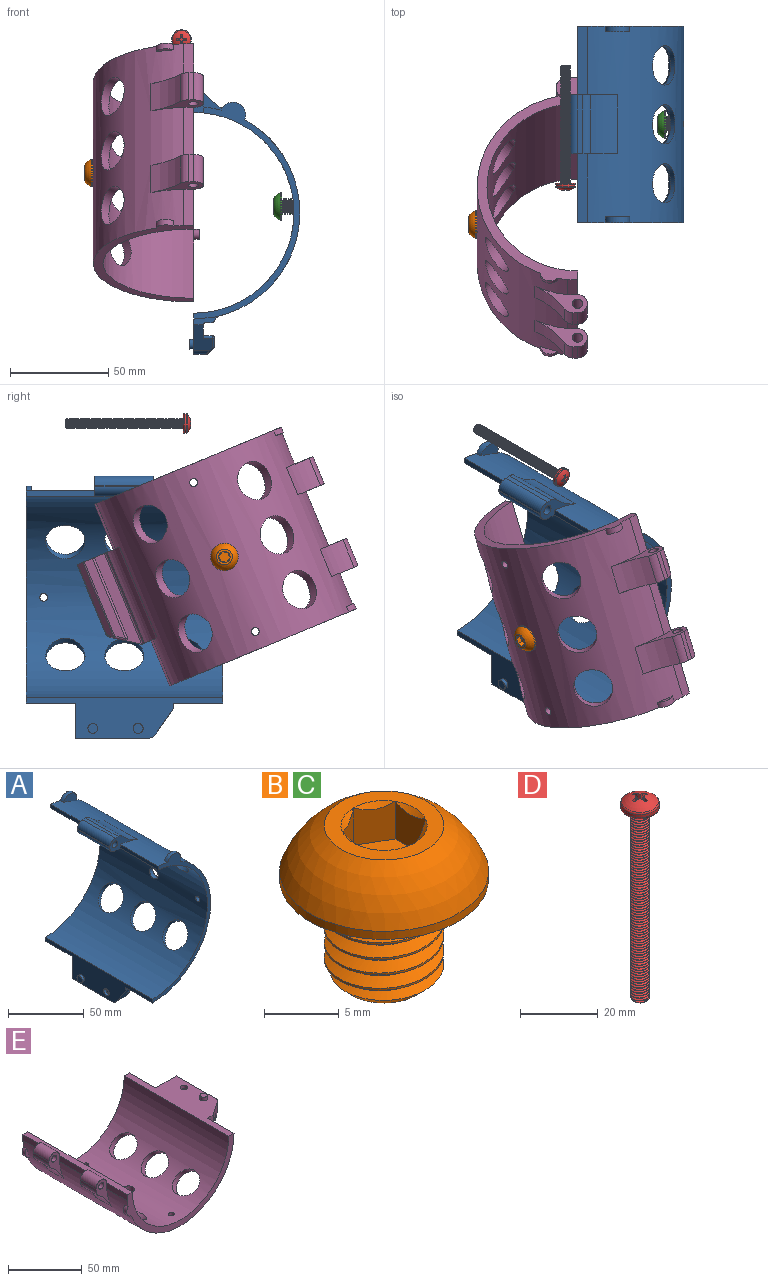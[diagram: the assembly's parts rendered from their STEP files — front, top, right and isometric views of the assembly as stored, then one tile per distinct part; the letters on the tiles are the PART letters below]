
ASSEMBLY  parts=5 mates=2
PART A: 58 faces, bbox 59.1x100x133.4 mm
  f0: cylinder r=54.1mm len=106.94mm, axis (0,1,0), area 12715.4mm2, adj f13,f14,f15,f16,f17,f18,f19,f23
  f1: cylinder r=51.1mm len=102.2mm, axis (0,1,0), area 13703.6mm2, adj f8,f10,f13,f14,f15,f16,f17,f18
  f2: plane 44.23x4.5mm, normal (0,0,1), area 199mm2, adj f3,f26,f28,f40
  f3: plane 50x7.07mm, normal (1,0,0), area 265.2mm2, adj f2,f26,f30,f32,f40
  f4: plane 50x3.5mm, normal (0,0,-1), area 175mm2, adj f24,f26,f29,f30
  f5: plane 36.89x6.59mm, normal (0,0,-1), area 243mm2, adj f8,f26,f33,f34
  f6: plane 41.02x2.91mm, normal (0.71,0,-0.71), area 163.9mm2, adj f26,f27,f34,f35,f36
  f7: plane 44.23x4.59mm, normal (1,0,0), area 195.4mm2, adj f26,f27,f28,f38
  f8: plane 100x20.84mm, normal (-1,0,0), area 1072.3mm2, adj f1,f5,f13,f14,f23,f24,f25,f26
  f9: cylinder r=2.55mm len=30mm, axis (0,1,0), area 480.7mm2, adj f16,f18
  f10: plane 30x0.02mm, normal (0,0,-1), area 0.6mm2, adj f1,f16,f18,f22
  f11: plane 30x2.74mm, normal (0,0,1), area 82.3mm2, adj f16,f18,f20,f21
  f12: plane 30x0.32mm, normal (-1,0,0), area 9.6mm2, adj f16,f18,f21,f22
  f13: plane 110.42x54.1mm, normal (0,-1,0), area 541.2mm2, adj f0,f1,f8,f15,f23,f46
  f14: plane 110.37x54.1mm, normal (0,1,0), area 540.6mm2, adj f0,f1,f8,f17,f25,f48
  f15: plane 35x3.01mm, normal (-1,0,0), area 105.5mm2, adj f0,f1,f13,f16
  f16: plane 25.52x11.37mm, normal (0,-1,0), area 109mm2, adj f0,f1,f9,f10,f11,f12,f15,f19
  f17: plane 35x3.01mm, normal (-1,0,0), area 105.5mm2, adj f0,f1,f14,f18
  f18: plane 25.52x11.37mm, normal (0,1,0), area 109mm2, adj f0,f1,f9,f10,f11,f12,f17,f19
  f19: cylinder r=40mm len=30mm, axis (0,-1,0), area 519.1mm2, adj f0,f16,f18,f20
  f20: cylinder r=5mm len=30mm, axis (0,-1,0), area 123.3mm2, adj f11,f16,f18,f19
  f21: cylinder r=5mm len=30mm, axis (0,1,0), area 235.6mm2, adj f11,f12,f16,f18
  f22: cylinder r=5mm len=30mm, axis (0,-1,0), area 235mm2, adj f10,f12,f16,f18
  f23: plane 25x10.5mm, normal (0.1,0,-1), area 263.8mm2, adj f0,f8,f13,f24
  f24: plane 13.81x4.63mm, normal (0,-1,0), area 31.6mm2, adj f0,f4,f8,f23,f29,f30,f31,f32
  f25: plane 25x10.5mm, normal (0.1,0,-1), area 263.8mm2, adj f0,f8,f14,f26
  f26: plane 19.63x13.81mm, normal (0,1,0), area 152.5mm2, adj f0,f2,f3,f4,f5,f6,f7,f8
  f27: cylinder r=1mm len=41.02mm, axis (0,1,0), area 32.2mm2, adj f6,f7,f26,f37
  f28: cylinder r=1mm len=44.23mm, axis (0,1,0), area 69.5mm2, adj f2,f7,f26,f39
  f29: cylinder r=1mm len=50mm, axis (0,-1,0), area 59.8mm2, adj f4,f24,f26,f31
  f30: cylinder r=1mm len=50mm, axis (0,-1,0), area 78.5mm2, adj f3,f4,f24,f26,f32
  f31: cylinder r=5mm len=50mm, axis (0,-1,0), area 234.3mm2, adj f0,f24,f26,f29
  f32: plane 12.87x9.5mm, normal (0,-0.82,-0.57), area 109.5mm2, adj f3,f8,f24,f30,f33,f36,f38,f40
  f33: cylinder r=5mm len=8.29mm, axis (-1,0,0), area 34.4mm2, adj f5,f8,f32,f35
  f34: cylinder r=1mm len=36.89mm, axis (0,1,0), area 29mm2, adj f5,f6,f26,f35
  f35: bspline ~4.44x2.86mm, area 4.4mm2, adj f6,f33,f34,f36
  f36: cylinder r=1mm len=1.92mm, axis (-0.63,0.44,-0.63), area 2.2mm2, adj f6,f32,f35,f37
  f37: sphere r=1mm, area 0.5mm2, adj f27,f36,f38
  f38: cylinder r=1mm len=5.16mm, axis (0,0.57,-0.82), area 8.8mm2, adj f7,f32,f37,f39
  f39: sphere r=1mm, area 2.2mm2, adj f28,f38,f40
  f40: cylinder r=1mm len=4.5mm, axis (1,0,0), area 9.8mm2, adj f2,f3,f32,f39
  f41: cylinder r=2.55mm len=5.1mm, axis (-1,0,0), area 32mm2, adj f8,f42
  f42: plane 5.1x5.1mm, normal (-1,0,0), area 20.4mm2, adj f41
  f43: cylinder r=2.5mm len=5mm, axis (1,0,0), area 31.4mm2, adj f8,f44
  f44: plane 5x5mm, normal (-1,0,0), area 19.6mm2, adj f43
  f45: cylinder r=4mm len=8mm, axis (-1,0,0), area 75.5mm2, adj f0,f1
  f46: cylinder r=6.46mm len=12.47mm, axis (0,-1,0), area 60.9mm2, adj f0,f13,f47
  f47: plane 12.47x8.87mm, normal (0,1,0), area 62.3mm2, adj f0,f46
  f48: cylinder r=6.47mm len=12.45mm, axis (0,1,0), area 60.6mm2, adj f0,f14,f49
  f49: plane 12.45x8.83mm, normal (0,-1,0), area 61.7mm2, adj f0,f48
  f50: cylinder r=2mm len=4mm, axis (-1,0,0), area 37.7mm2, adj f0,f1
  f51: cylinder r=2mm len=4mm, axis (-1,0,0), area 37.7mm2, adj f0,f1
  f52: cylinder r=10mm len=20mm, axis (-0.71,0,-0.71), area 193.9mm2, adj f0,f1
  f53: cylinder r=10mm len=20mm, axis (-0.71,0,-0.71), area 193.9mm2, adj f0,f1
  f54: cylinder r=10mm len=20mm, axis (-0.71,0,-0.71), area 193.9mm2, adj f0,f1
  f55: cylinder r=10mm len=20mm, axis (-0.71,0,0.71), area 192.6mm2, adj f0,f1
  f56: cylinder r=10mm len=20mm, axis (-0.71,0,0.71), area 192.6mm2, adj f0,f1
  f57: cylinder r=10mm len=20mm, axis (-0.71,0,0.71), area 192.6mm2, adj f0,f1
PART B: 24 faces, bbox 15.1x15.1x13.8 mm
  f0: cylinder r=4mm len=8mm, axis (0,0,-1), area 22.4mm2, adj f1,f5,f22,f23
  f1: bspline ~8.81x8mm, area 126.7mm2, adj f0,f2,f4,f5,f23
  f2: cone r=3.06mm half-angle=45deg, axis (0,0,1), area 12.7mm2, adj f1,f3,f4,f23
  f3: plane 6.13x6.13mm, normal (0,0,-1), area 29.5mm2, adj f2
  f4: cylinder r=3.19mm len=7.87mm, axis (0,0,-1), area 19.9mm2, adj f1,f2,f5,f22
  f5: plane 14.51x14.51mm, normal (0,0,-1), area 113.1mm2, adj f0,f1,f4,f6,f22
  f6: cylinder r=7mm len=14mm, axis (0,0,1), area 29mm2, adj f5,f7
  f7: sphere r=7.45mm, area 175mm2, adj f6,f8
  f8: plane 8.94x8.94mm, normal (0,0,1), area 24.1mm2, adj f7,f9,f17,f18,f19,f20,f21
  f9: cone r=2.89mm half-angle=45deg, axis (0,0,1), area 0mm2, adj f8,f10
  f10: plane 4.17x3.59mm, normal (0.5,0.87,0), area 8.2mm2, adj f9,f11,f15,f16
  f11: plane 5.77x5mm, normal (0,0,1), area 21.7mm2, adj f10,f12,f13,f14,f15,f16
  f12: plane 4.17x3.59mm, normal (0.5,-0.87,0), area 8.2mm2, adj f11,f13,f16,f20
  f13: plane 4.17x3.59mm, normal (-0.5,-0.87,0), area 8.2mm2, adj f11,f12,f14,f19
  f14: plane 4.18x3.99mm, normal (-1,0,0), area 8.2mm2, adj f11,f13,f15,f18
  f15: plane 4.17x3.59mm, normal (-0.5,0.87,0), area 8.2mm2, adj f10,f11,f14,f17
  f16: plane 4.18x3.99mm, normal (1,0,0), area 8.2mm2, adj f10,f11,f12,f21
  f17: cone r=2.89mm half-angle=45deg, axis (0,0,1), area 0mm2, adj f8,f15
  f18: cone r=2.89mm half-angle=45deg, axis (0,0,1), area 0mm2, adj f8,f14
  f19: cone r=2.89mm half-angle=45deg, axis (0,0,1), area 0mm2, adj f8,f13
  f20: cone r=2.89mm half-angle=45deg, axis (0,0,1), area 0mm2, adj f8,f12
  f21: cone r=2.89mm half-angle=45deg, axis (0,0,1), area 0mm2, adj f8,f16
  f22: bspline ~8.59x8mm, area 126.7mm2, adj f0,f4,f5,f23
  f23: cone r=3.06mm half-angle=45deg, axis (0,0,1), area 3.4mm2, adj f0,f1,f2,f22
PART C: same geometry as B
PART D: 182 faces, bbox 11.1x11.1x64.3 mm
  f0: cylinder r=2.5mm len=5mm, axis (0,0,1), area 0.8mm2, adj f75,f76,f150,f151
  f1: cylinder r=2.5mm len=5mm, axis (0,0,1), area 0.8mm2, adj f76,f77,f150,f151
  f2: cylinder r=2.5mm len=5mm, axis (0,0,1), area 0.8mm2, adj f77,f78,f150,f151
  f3: cylinder r=2.5mm len=5mm, axis (0,0,1), area 0.8mm2, adj f78,f79,f150,f151
  f4: cylinder r=2.5mm len=5mm, axis (0,0,1), area 0.8mm2, adj f79,f80,f150,f151
  f5: cylinder r=2.5mm len=5mm, axis (0,0,1), area 0.8mm2, adj f80,f81,f150,f151
  f6: cylinder r=2.5mm len=5mm, axis (0,0,1), area 0.8mm2, adj f81,f82,f150,f151
  f7: cylinder r=2.5mm len=5mm, axis (0,0,1), area 0.8mm2, adj f82,f83,f150,f151
  f8: cylinder r=2.5mm len=5mm, axis (0,0,1), area 0.8mm2, adj f83,f84,f150,f151
  f9: cylinder r=2.5mm len=5mm, axis (0,0,1), area 0.8mm2, adj f84,f85,f150,f151
  f10: cylinder r=2.5mm len=5mm, axis (0,0,1), area 0.8mm2, adj f85,f86,f150,f151
  f11: cylinder r=2.5mm len=5mm, axis (0,0,1), area 0.8mm2, adj f86,f87,f150,f151
  f12: cylinder r=2.5mm len=5mm, axis (0,0,1), area 0.8mm2, adj f87,f88,f150,f151
  f13: cylinder r=2.5mm len=5mm, axis (0,0,1), area 0.8mm2, adj f88,f89,f150,f151
  f14: cylinder r=2.5mm len=5mm, axis (0,0,1), area 0.8mm2, adj f89,f90,f150,f151
  f15: cylinder r=2.5mm len=5mm, axis (0,0,1), area 0.8mm2, adj f90,f91,f150,f151
  f16: cylinder r=2.5mm len=5mm, axis (0,0,1), area 0.8mm2, adj f91,f92,f150,f151
  f17: cylinder r=2.5mm len=5mm, axis (0,0,1), area 0.8mm2, adj f92,f93,f150,f151
  f18: cylinder r=2.5mm len=5mm, axis (0,0,1), area 0.8mm2, adj f93,f94,f150,f151
  f19: cylinder r=2.5mm len=5mm, axis (0,0,1), area 0.8mm2, adj f94,f95,f150,f151
  f20: cylinder r=2.5mm len=5mm, axis (0,0,1), area 0.8mm2, adj f95,f96,f150,f151
  f21: cylinder r=2.5mm len=5mm, axis (0,0,1), area 0.8mm2, adj f96,f97,f150,f151
  f22: cylinder r=2.5mm len=5mm, axis (0,0,1), area 0.8mm2, adj f97,f98,f150,f151
  f23: cylinder r=2.5mm len=5mm, axis (0,0,1), area 0.8mm2, adj f98,f99,f150,f151
  f24: cylinder r=2.5mm len=5mm, axis (0,0,1), area 0.8mm2, adj f99,f100,f150,f151
  f25: cylinder r=2.5mm len=5mm, axis (0,0,1), area 0.8mm2, adj f100,f101,f150,f151
  f26: cylinder r=2.5mm len=5mm, axis (0,0,1), area 0.8mm2, adj f101,f102,f150,f151
  f27: cylinder r=2.5mm len=5mm, axis (0,0,1), area 0.8mm2, adj f102,f103,f150,f151
  f28: cylinder r=2.5mm len=5mm, axis (0,0,1), area 0.8mm2, adj f103,f104,f150,f151
  f29: cylinder r=2.5mm len=5mm, axis (0,0,1), area 0.8mm2, adj f104,f105,f150,f151
  f30: cylinder r=2.5mm len=5mm, axis (0,0,1), area 0.8mm2, adj f105,f106,f150,f151
  f31: cylinder r=2.5mm len=5mm, axis (0,0,1), area 0.8mm2, adj f106,f107,f150,f151
  f32: cylinder r=2.5mm len=5mm, axis (0,0,1), area 0.8mm2, adj f107,f108,f150,f151
  f33: cylinder r=2.5mm len=5mm, axis (0,0,1), area 0.8mm2, adj f108,f109,f150,f151
  f34: cylinder r=2.5mm len=5mm, axis (0,0,1), area 0.8mm2, adj f109,f110,f150,f151
  f35: cylinder r=2.5mm len=5mm, axis (0,0,1), area 0.8mm2, adj f110,f111,f150,f151
  f36: cylinder r=2.5mm len=5mm, axis (0,0,1), area 0.8mm2, adj f111,f112,f150,f151
  f37: cylinder r=2.5mm len=5mm, axis (0,0,1), area 0.8mm2, adj f112,f113,f150,f151
  f38: cylinder r=2.5mm len=5mm, axis (0,0,1), area 0.8mm2, adj f113,f114,f150,f151
  f39: cylinder r=2.5mm len=5mm, axis (0,0,1), area 0.8mm2, adj f114,f115,f150,f151
  f40: cylinder r=2.5mm len=5mm, axis (0,0,1), area 0.8mm2, adj f115,f116,f150,f151
  f41: cylinder r=2.5mm len=5mm, axis (0,0,1), area 0.8mm2, adj f116,f117,f150,f151
  f42: cylinder r=2.5mm len=5mm, axis (0,0,1), area 0.8mm2, adj f117,f118,f150,f151
  f43: cylinder r=2.5mm len=5mm, axis (0,0,1), area 0.8mm2, adj f118,f119,f150,f151
  f44: cylinder r=2.5mm len=5mm, axis (0,0,1), area 0.8mm2, adj f119,f120,f150,f151
  f45: cylinder r=2.5mm len=5mm, axis (0,0,1), area 0.8mm2, adj f120,f121,f150,f151
  f46: cylinder r=2.5mm len=5mm, axis (0,0,1), area 0.8mm2, adj f121,f122,f150,f151
  f47: cylinder r=2.5mm len=5mm, axis (0,0,1), area 0.8mm2, adj f122,f123,f150,f151
  f48: cylinder r=2.5mm len=5mm, axis (0,0,1), area 0.8mm2, adj f123,f124,f150,f151
  f49: cylinder r=2.5mm len=5mm, axis (0,0,1), area 0.8mm2, adj f124,f125,f150,f151
  f50: cylinder r=2.5mm len=5mm, axis (0,0,1), area 0.8mm2, adj f125,f126,f150,f151
  f51: cylinder r=2.5mm len=5mm, axis (0,0,1), area 0.8mm2, adj f126,f127,f150,f151
  f52: cylinder r=2.5mm len=5mm, axis (0,0,1), area 0.8mm2, adj f127,f128,f150,f151
  f53: cylinder r=2.5mm len=5mm, axis (0,0,1), area 0.8mm2, adj f128,f129,f150,f151
  f54: cylinder r=2.5mm len=5mm, axis (0,0,1), area 0.8mm2, adj f129,f130,f150,f151
  f55: cylinder r=2.5mm len=5mm, axis (0,0,1), area 0.8mm2, adj f130,f131,f150,f151
  f56: cylinder r=2.5mm len=5mm, axis (0,0,1), area 0.8mm2, adj f131,f132,f150,f151
  f57: cylinder r=2.5mm len=5mm, axis (0,0,1), area 0.8mm2, adj f132,f133,f150,f151
  f58: cylinder r=2.5mm len=5mm, axis (0,0,1), area 0.8mm2, adj f133,f134,f150,f151
  f59: cylinder r=2.5mm len=5mm, axis (0,0,1), area 0.8mm2, adj f134,f135,f150,f151
  f60: cylinder r=2.5mm len=5mm, axis (0,0,1), area 0.8mm2, adj f135,f136,f150,f151
  f61: cylinder r=2.5mm len=5mm, axis (0,0,1), area 0.8mm2, adj f136,f137,f150,f151
  f62: cylinder r=2.5mm len=5mm, axis (0,0,1), area 0.8mm2, adj f137,f138,f150,f151
  f63: cylinder r=2.5mm len=5mm, axis (0,0,1), area 0.8mm2, adj f138,f139,f150,f151
  f64: cylinder r=2.5mm len=5mm, axis (0,0,1), area 0.8mm2, adj f139,f140,f150,f151
  f65: cylinder r=2.5mm len=5mm, axis (0,0,1), area 0.8mm2, adj f140,f141,f150,f151
  f66: cylinder r=2.5mm len=5mm, axis (0,0,1), area 0.8mm2, adj f141,f142,f150,f151
  f67: cylinder r=2.5mm len=5mm, axis (0,0,1), area 0.8mm2, adj f142,f143,f150,f151
  f68: cylinder r=2.5mm len=5mm, axis (0,0,1), area 0.8mm2, adj f143,f144,f150,f151
  f69: cylinder r=2.5mm len=5mm, axis (0,0,1), area 0.8mm2, adj f144,f145,f150,f151
  f70: cylinder r=2.5mm len=5mm, axis (0,0,1), area 0.8mm2, adj f145,f146,f150,f151
  f71: cylinder r=2.5mm len=5mm, axis (0,0,1), area 0.8mm2, adj f146,f147,f150,f151
  f72: cylinder r=2.5mm len=5mm, axis (0,0,1), area 0.8mm2, adj f147,f148,f150,f151
  f73: cylinder r=2.5mm len=5mm, axis (0,0,1), area 0.8mm2, adj f148,f150,f151,f152
  f74: cylinder r=2.5mm len=0.97mm, axis (0,0,1), area 0mm2, adj f75,f149,f151
  f75: cylinder r=2.5mm len=5mm, axis (0,0,1), area 0.8mm2, adj f0,f74,f149,f150,f151
  f76: cylinder r=2.5mm len=5mm, axis (0,0,1), area 0.8mm2, adj f0,f1,f150,f151
  f77: cylinder r=2.5mm len=5mm, axis (0,0,1), area 0.8mm2, adj f1,f2,f150,f151
  f78: cylinder r=2.5mm len=5mm, axis (0,0,1), area 0.8mm2, adj f2,f3,f150,f151
  f79: cylinder r=2.5mm len=5mm, axis (0,0,1), area 0.8mm2, adj f3,f4,f150,f151
  f80: cylinder r=2.5mm len=5mm, axis (0,0,1), area 0.8mm2, adj f4,f5,f150,f151
  f81: cylinder r=2.5mm len=5mm, axis (0,0,1), area 0.8mm2, adj f5,f6,f150,f151
  f82: cylinder r=2.5mm len=5mm, axis (0,0,1), area 0.8mm2, adj f6,f7,f150,f151
  f83: cylinder r=2.5mm len=5mm, axis (0,0,1), area 0.8mm2, adj f7,f8,f150,f151
  f84: cylinder r=2.5mm len=5mm, axis (0,0,1), area 0.8mm2, adj f8,f9,f150,f151
  f85: cylinder r=2.5mm len=5mm, axis (0,0,1), area 0.8mm2, adj f9,f10,f150,f151
  f86: cylinder r=2.5mm len=5mm, axis (0,0,1), area 0.8mm2, adj f10,f11,f150,f151
  f87: cylinder r=2.5mm len=5mm, axis (0,0,1), area 0.8mm2, adj f11,f12,f150,f151
  f88: cylinder r=2.5mm len=5mm, axis (0,0,1), area 0.8mm2, adj f12,f13,f150,f151
  f89: cylinder r=2.5mm len=5mm, axis (0,0,1), area 0.8mm2, adj f13,f14,f150,f151
  f90: cylinder r=2.5mm len=5mm, axis (0,0,1), area 0.8mm2, adj f14,f15,f150,f151
  f91: cylinder r=2.5mm len=5mm, axis (0,0,1), area 0.8mm2, adj f15,f16,f150,f151
  f92: cylinder r=2.5mm len=5mm, axis (0,0,1), area 0.8mm2, adj f16,f17,f150,f151
  f93: cylinder r=2.5mm len=5mm, axis (0,0,1), area 0.8mm2, adj f17,f18,f150,f151
  f94: cylinder r=2.5mm len=5mm, axis (0,0,1), area 0.8mm2, adj f18,f19,f150,f151
  f95: cylinder r=2.5mm len=5mm, axis (0,0,1), area 0.8mm2, adj f19,f20,f150,f151
  f96: cylinder r=2.5mm len=5mm, axis (0,0,1), area 0.8mm2, adj f20,f21,f150,f151
  f97: cylinder r=2.5mm len=5mm, axis (0,0,1), area 0.8mm2, adj f21,f22,f150,f151
  f98: cylinder r=2.5mm len=5mm, axis (0,0,1), area 0.8mm2, adj f22,f23,f150,f151
  f99: cylinder r=2.5mm len=5mm, axis (0,0,1), area 0.8mm2, adj f23,f24,f150,f151
  f100: cylinder r=2.5mm len=5mm, axis (0,0,1), area 0.8mm2, adj f24,f25,f150,f151
  f101: cylinder r=2.5mm len=5mm, axis (0,0,1), area 0.8mm2, adj f25,f26,f150,f151
  f102: cylinder r=2.5mm len=5mm, axis (0,0,1), area 0.8mm2, adj f26,f27,f150,f151
  f103: cylinder r=2.5mm len=5mm, axis (0,0,1), area 0.8mm2, adj f27,f28,f150,f151
  f104: cylinder r=2.5mm len=5mm, axis (0,0,1), area 0.8mm2, adj f28,f29,f150,f151
  f105: cylinder r=2.5mm len=5mm, axis (0,0,1), area 0.8mm2, adj f29,f30,f150,f151
  f106: cylinder r=2.5mm len=5mm, axis (0,0,1), area 0.8mm2, adj f30,f31,f150,f151
  f107: cylinder r=2.5mm len=5mm, axis (0,0,1), area 0.8mm2, adj f31,f32,f150,f151
  f108: cylinder r=2.5mm len=5mm, axis (0,0,1), area 0.8mm2, adj f32,f33,f150,f151
  f109: cylinder r=2.5mm len=5mm, axis (0,0,1), area 0.8mm2, adj f33,f34,f150,f151
  f110: cylinder r=2.5mm len=5mm, axis (0,0,1), area 0.8mm2, adj f34,f35,f150,f151
  f111: cylinder r=2.5mm len=5mm, axis (0,0,1), area 0.8mm2, adj f35,f36,f150,f151
  f112: cylinder r=2.5mm len=5mm, axis (0,0,1), area 0.8mm2, adj f36,f37,f150,f151
  f113: cylinder r=2.5mm len=5mm, axis (0,0,1), area 0.8mm2, adj f37,f38,f150,f151
  f114: cylinder r=2.5mm len=5mm, axis (0,0,1), area 0.8mm2, adj f38,f39,f150,f151
  f115: cylinder r=2.5mm len=5mm, axis (0,0,1), area 0.8mm2, adj f39,f40,f150,f151
  f116: cylinder r=2.5mm len=5mm, axis (0,0,1), area 0.8mm2, adj f40,f41,f150,f151
  f117: cylinder r=2.5mm len=5mm, axis (0,0,1), area 0.8mm2, adj f41,f42,f150,f151
  f118: cylinder r=2.5mm len=5mm, axis (0,0,1), area 0.8mm2, adj f42,f43,f150,f151
  f119: cylinder r=2.5mm len=5mm, axis (0,0,1), area 0.8mm2, adj f43,f44,f150,f151
  f120: cylinder r=2.5mm len=5mm, axis (0,0,1), area 0.8mm2, adj f44,f45,f150,f151
  f121: cylinder r=2.5mm len=5mm, axis (0,0,1), area 0.8mm2, adj f45,f46,f150,f151
  f122: cylinder r=2.5mm len=5mm, axis (0,0,1), area 0.8mm2, adj f46,f47,f150,f151
  f123: cylinder r=2.5mm len=5mm, axis (0,0,1), area 0.8mm2, adj f47,f48,f150,f151
  f124: cylinder r=2.5mm len=5mm, axis (0,0,1), area 0.8mm2, adj f48,f49,f150,f151
  f125: cylinder r=2.5mm len=5mm, axis (0,0,1), area 0.8mm2, adj f49,f50,f150,f151
  f126: cylinder r=2.5mm len=5mm, axis (0,0,1), area 0.8mm2, adj f50,f51,f150,f151
  f127: cylinder r=2.5mm len=5mm, axis (0,0,1), area 0.8mm2, adj f51,f52,f150,f151
  f128: cylinder r=2.5mm len=5mm, axis (0,0,1), area 0.8mm2, adj f52,f53,f150,f151
  f129: cylinder r=2.5mm len=5mm, axis (0,0,1), area 0.8mm2, adj f53,f54,f150,f151
  f130: cylinder r=2.5mm len=5mm, axis (0,0,1), area 0.8mm2, adj f54,f55,f150,f151
  f131: cylinder r=2.5mm len=5mm, axis (0,0,1), area 0.8mm2, adj f55,f56,f150,f151
  f132: cylinder r=2.5mm len=5mm, axis (0,0,1), area 0.8mm2, adj f56,f57,f150,f151
  f133: cylinder r=2.5mm len=5mm, axis (0,0,1), area 0.8mm2, adj f57,f58,f150,f151
  f134: cylinder r=2.5mm len=5mm, axis (0,0,1), area 0.8mm2, adj f58,f59,f150,f151
  f135: cylinder r=2.5mm len=5mm, axis (0,0,1), area 0.8mm2, adj f59,f60,f150,f151
  f136: cylinder r=2.5mm len=5mm, axis (0,0,1), area 0.8mm2, adj f60,f61,f150,f151
  f137: cylinder r=2.5mm len=5mm, axis (0,0,1), area 0.8mm2, adj f61,f62,f150,f151
  f138: cylinder r=2.5mm len=5mm, axis (0,0,1), area 0.8mm2, adj f62,f63,f150,f151
  f139: cylinder r=2.5mm len=5mm, axis (0,0,1), area 0.8mm2, adj f63,f64,f150,f151
  f140: cylinder r=2.5mm len=5mm, axis (0,0,1), area 0.8mm2, adj f64,f65,f150,f151
  f141: cylinder r=2.5mm len=5mm, axis (0,0,1), area 0.8mm2, adj f65,f66,f150,f151
  f142: cylinder r=2.5mm len=5mm, axis (0,0,1), area 0.8mm2, adj f66,f67,f150,f151
  f143: cylinder r=2.5mm len=5mm, axis (0,0,1), area 0.8mm2, adj f67,f68,f150,f151
  f144: cylinder r=2.5mm len=5mm, axis (0,0,1), area 0.8mm2, adj f68,f69,f150,f151
  f145: cylinder r=2.5mm len=5mm, axis (0,0,1), area 0.8mm2, adj f69,f70,f150,f151
  f146: cylinder r=2.5mm len=5mm, axis (0,0,1), area 0.8mm2, adj f70,f71,f150,f151
  f147: cylinder r=2.5mm len=5mm, axis (0,0,1), area 0.8mm2, adj f71,f72,f150,f151
  f148: cylinder r=2.5mm len=5mm, axis (0,0,1), area 0.8mm2, adj f72,f73,f150,f151
  f149: plane 8.91x8.91mm, normal (0,0,-1), area 42.2mm2, adj f74,f75,f150,f151,f155,f157
  f150: bspline ~60.3x5.77mm, area 630mm2, adj f0,f1,f2,f3,f4,f5,f6,f7
  f151: bspline ~60.43x5.77mm, area 631.3mm2, adj f0,f1,f2,f3,f4,f5,f6,f7
  f152: cylinder r=2.5mm len=4.64mm, axis (0,0,1), area 0.6mm2, adj f73,f150,f151,f156
  f153: bspline ~4.44x2.57mm, area 0.7mm2, adj f150,f155,f156
  f154: plane 3.96x3.96mm, normal (0,0,-1), area 12.3mm2, adj f155,f156
  f155: cylinder r=1.98mm len=60mm, axis (0,0,1), area -435.6mm2, adj f149,f150,f151,f153,f154
  f156: cone r=5.16mm half-angle=45deg, axis (0,0,1), area 5mm2, adj f150,f151,f152,f153,f154
  f157: torus R=4.3mm, axis (0,0,1), area 32.9mm2, adj f149,f158
  f158: cylinder r=5mm len=10mm, axis (0,0,-1), area 29.2mm2, adj f157,f160
  f159: sphere r=7.39mm, area 70.7mm2, adj f160,f161,f162,f163,f164,f165,f166,f168
  f160: torus R=4.3mm, axis (0,0,1), area 18.9mm2, adj f158,f159
  f161: cone r=2.5mm half-angle=15deg, axis (0,0,1), area 2mm2, adj f159,f162,f167,f181
  f162: plane 3.29x1.25mm, normal (-1,0,0.09), area 2.4mm2, adj f159,f161,f163,f167
  f163: plane 3.33x0.83mm, normal (-0.92,-0.38,0.09), area 2.2mm2, adj f159,f162,f164,f167
  f164: plane 3.33x0.83mm, normal (-0.38,-0.92,0.09), area 2.2mm2, adj f159,f163,f165,f167
  f165: plane 3.29x1.25mm, normal (0,-1,0.09), area 2.4mm2, adj f159,f164,f166,f167
  f166: cone r=2.5mm half-angle=15deg, axis (0,0,1), area 2mm2, adj f159,f165,f167,f168
  f167: plane 3.22x3.22mm, normal (0,0,1), area 3.7mm2, adj f161,f162,f163,f164,f165,f166,f168,f169
  f168: plane 3.29x1.25mm, normal (0,1,0.09), area 2.4mm2, adj f159,f166,f167,f169
  f169: plane 3.33x0.83mm, normal (-0.38,0.92,0.09), area 2.2mm2, adj f159,f167,f168,f170
  f170: plane 3.33x0.83mm, normal (-0.92,0.38,0.09), area 2.2mm2, adj f159,f167,f169,f171
  f171: plane 3.29x1.25mm, normal (-1,0,0.09), area 2.4mm2, adj f159,f167,f170,f172
  f172: cone r=2.5mm half-angle=15deg, axis (0,0,1), area 2mm2, adj f159,f167,f171,f173
  f173: plane 3.29x1.25mm, normal (1,0,0.09), area 2.4mm2, adj f159,f167,f172,f174
  f174: plane 3.33x0.83mm, normal (0.92,0.38,0.09), area 2.2mm2, adj f159,f167,f173,f175
  f175: plane 3.33x0.83mm, normal (0.38,0.92,0.09), area 2.2mm2, adj f159,f167,f174,f176
  f176: plane 3.29x1.25mm, normal (0,1,0.09), area 2.4mm2, adj f159,f167,f175,f177
  f177: cone r=2.5mm half-angle=15deg, axis (0,0,1), area 2mm2, adj f159,f167,f176,f178
  f178: plane 3.29x1.25mm, normal (0,-1,0.09), area 2.4mm2, adj f159,f167,f177,f179
  f179: plane 3.33x0.83mm, normal (0.38,-0.92,0.09), area 2.2mm2, adj f159,f167,f178,f180
  f180: plane 3.33x0.83mm, normal (0.92,-0.38,0.09), area 2.2mm2, adj f159,f167,f179,f181
  f181: plane 3.29x1.25mm, normal (1,0,0.09), area 2.4mm2, adj f159,f161,f167,f180
PART E: 64 faces, bbox 132x100x56.1 mm
  f0: cylinder r=51.1mm len=100.86mm, axis (0,1,0), area 11498.3mm2, adj f2,f6,f7,f8,f16,f17,f18,f19
  f1: cylinder r=46.1mm len=100mm, axis (0,1,0), area 12471.8mm2, adj f2,f8,f15,f21,f37,f38,f39,f58
  f2: plane 102.73x51.1mm, normal (0,-1,0), area 777.7mm2, adj f0,f1,f15,f16,f21,f29,f43
  f3: cylinder r=2.55mm len=15mm, axis (0,-1,0), area 240.3mm2, adj f42,f44
  f4: plane 15x2.37mm, normal (-1,0,0), area 35.6mm2, adj f20,f27,f28,f40
  f5: cylinder r=2.55mm len=15mm, axis (0,1,0), area 240.3mm2, adj f20,f40
  f6: cylinder r=40mm len=15.27mm, axis (0,-1,0), area 299.5mm2, adj f0,f20,f27,f40
  f7: plane 30x5mm, normal (-1,0,0), area 150mm2, adj f0,f20,f21,f42
  f8: plane 102.73x51.1mm, normal (0,1,0), area 777.7mm2, adj f0,f1,f15,f18,f21,f22,f31
  f9: plane 44.21x4.5mm, normal (-1,0,0), area 198.9mm2, adj f10,f19,f26,f57
  f10: plane 49.98x7.07mm, normal (0,0,-1), area 265.1mm2, adj f9,f19,f24,f48,f57
  f11: plane 50x3.88mm, normal (1,0,0), area 194.2mm2, adj f17,f19,f24,f25
  f12: plane 37.92x6.59mm, normal (1,0,0), area 249.7mm2, adj f15,f19,f49,f50
  f13: plane 41x2.91mm, normal (0.71,0,-0.71), area 164.5mm2, adj f19,f50,f51,f52,f53
  f14: plane 44.21x4.59mm, normal (0,0,-1), area 195.4mm2, adj f19,f26,f53,f55
  f15: plane 100x25mm, normal (0,0,1), area 1380.5mm2, adj f1,f2,f8,f12,f16,f17,f18,f19
  f16: plane 25x10.5mm, normal (0.99,0,-0.1), area 263.9mm2, adj f0,f2,f15,f17
  f17: plane 18.58x8.47mm, normal (0,-1,0), area 64.6mm2, adj f0,f11,f15,f16,f23,f24,f25,f48
  f18: plane 25x10.5mm, normal (0.99,0,-0.1), area 263.9mm2, adj f0,f8,f15,f19
  f19: plane 23.5x18.58mm, normal (0,1,0), area 185.6mm2, adj f0,f9,f10,f11,f12,f13,f14,f15
  f20: plane 26.67x14.58mm, normal (0,-1,0), area 119.5mm2, adj f0,f4,f5,f6,f7,f27,f28
  f21: plane 100x4.75mm, normal (0,0,1), area 475.5mm2, adj f1,f2,f7,f8,f22,f28,f43,f46
  f22: plane 20x5mm, normal (-1,0,0), area 100mm2, adj f0,f8,f21,f40
  f23: cylinder r=15mm len=50mm, axis (0,-1,0), area 534.3mm2, adj f0,f17,f19,f25
  f24: cylinder r=1mm len=50mm, axis (0,-1,0), area 78.5mm2, adj f10,f11,f17,f19,f48
  f25: cylinder r=1mm len=50mm, axis (0,-1,0), area 54.2mm2, adj f11,f17,f19,f23
  f26: cylinder r=1mm len=44.21mm, axis (0,1,0), area 69.4mm2, adj f9,f14,f19,f56
  f27: cylinder r=5mm len=15mm, axis (0,-1,0), area 70.3mm2, adj f4,f6,f20,f40
  f28: cylinder r=5mm len=15mm, axis (0,1,0), area 235.6mm2, adj f4,f20,f21,f40
  f29: cylinder r=5mm len=8.61mm, axis (0,-1,0), area 33.6mm2, adj f0,f2,f30
  f30: plane 8.61x4.22mm, normal (0,1,0), area 17mm2, adj f0,f29
  f31: cylinder r=5mm len=8.61mm, axis (0,1,0), area 33.6mm2, adj f0,f8,f32
  f32: plane 8.61x4.22mm, normal (0,-1,0), area 17mm2, adj f0,f31
  f33: cylinder r=2.55mm len=5.1mm, axis (0,0,1), area 48.1mm2, adj f15,f34
  f34: plane 5.1x5.1mm, normal (0,0,1), area 20.4mm2, adj f33
  f35: cylinder r=2.5mm len=5mm, axis (0,0,-1), area 47.1mm2, adj f15,f36
  f36: plane 5x5mm, normal (0,0,1), area 19.6mm2, adj f35
  f37: cylinder r=4mm len=8mm, axis (0,0,1), area 125.9mm2, adj f0,f1
  f38: cylinder r=2mm len=5.01mm, axis (0,0,1), area 62.9mm2, adj f0,f1
  f39: cylinder r=2mm len=5.01mm, axis (0,0,1), area 62.9mm2, adj f0,f1
  f40: plane 26.67x14.58mm, normal (0,1,0), area 119.5mm2, adj f0,f4,f5,f6,f22,f27,f28
  f41: plane 15x2.37mm, normal (-1,0,0), area 35.6mm2, adj f42,f44,f46,f47
  f42: plane 26.67x14.58mm, normal (0,1,0), area 119.5mm2, adj f0,f3,f7,f41,f45,f46,f47
  f43: plane 20x5mm, normal (-1,0,0), area 100mm2, adj f0,f2,f21,f44
  f44: plane 26.67x14.58mm, normal (0,-1,0), area 119.5mm2, adj f0,f3,f41,f43,f45,f46,f47
  f45: cylinder r=40mm len=15.27mm, axis (0,-1,0), area 299.5mm2, adj f0,f42,f44,f47
  f46: cylinder r=5mm len=15mm, axis (0,-1,0), area 235.6mm2, adj f21,f41,f42,f44
  f47: cylinder r=5mm len=15mm, axis (0,-1,0), area 70.3mm2, adj f41,f42,f44,f45
  f48: plane 13.75x9.63mm, normal (0.57,-0.82,0), area 117.8mm2, adj f10,f15,f17,f24,f49,f52,f55,f57
  f49: cylinder r=3mm len=7.44mm, axis (0,0,-1), area 19.8mm2, adj f12,f15,f48,f51
  f50: cylinder r=1mm len=37.92mm, axis (0,1,0), area 29.8mm2, adj f12,f13,f19,f51
  f51: bspline ~2.79x1.78mm, area 2.4mm2, adj f13,f49,f50,f52
  f52: cylinder r=1mm len=2.77mm, axis (-0.63,-0.44,-0.63), area 3.8mm2, adj f13,f48,f51,f54
  f53: cylinder r=1mm len=41mm, axis (0,1,0), area 32.2mm2, adj f13,f14,f19,f54
  f54: sphere r=1mm, area 0.5mm2, adj f52,f53,f55
  f55: cylinder r=1mm len=5.16mm, axis (-0.82,-0.57,0), area 8.8mm2, adj f14,f48,f54,f56
  f56: sphere r=1mm, area 2.2mm2, adj f26,f55,f57
  f57: cylinder r=1mm len=4.5mm, axis (0,0,1), area 9.8mm2, adj f9,f10,f48,f56
  f58: cylinder r=10mm len=20.54mm, axis (-0.71,0,0.71), area 323.6mm2, adj f0,f1
  f59: cylinder r=10mm len=20.54mm, axis (-0.71,0,0.71), area 323.6mm2, adj f0,f1
  f60: cylinder r=10mm len=20.54mm, axis (-0.71,0,0.71), area 323.6mm2, adj f0,f1
  f61: cylinder r=10mm len=20.54mm, axis (0.71,0,0.71), area 323.6mm2, adj f0,f1
  f62: cylinder r=10mm len=20.54mm, axis (0.71,0,0.71), area 323.6mm2, adj f0,f1
  f63: cylinder r=10mm len=20.54mm, axis (0.71,0,0.71), area 323.6mm2, adj f0,f1
PLACE A t=(-37.01,-17.05,-2.57)mm fixed
PLACE B rot(axis=(0.49,-0.73,-0.49),108deg) t=(-92.72,-118,-36.39)mm
PLACE C rot(axis=(-0.49,-0.73,0.49),108deg) t=(3.5,-67.05,-53.42)mm
PLACE D rot(axis=(0,-0.71,0.71),180deg) t=(-43.16,-37.03,31.47)mm
PLACE E rot(axis=(0.49,0.73,0.49),108deg) t=(-44.5,-124.77,20.51)mm
MATE cylindrical E.f37 <-> B.f0  axis (1,0,0) through (-88.15,-118,-36.39)mm
MATE planar A.f8 <-> E.f15  axis (-1,0,0) through (-37.01,-65.61,-116.34)mm
